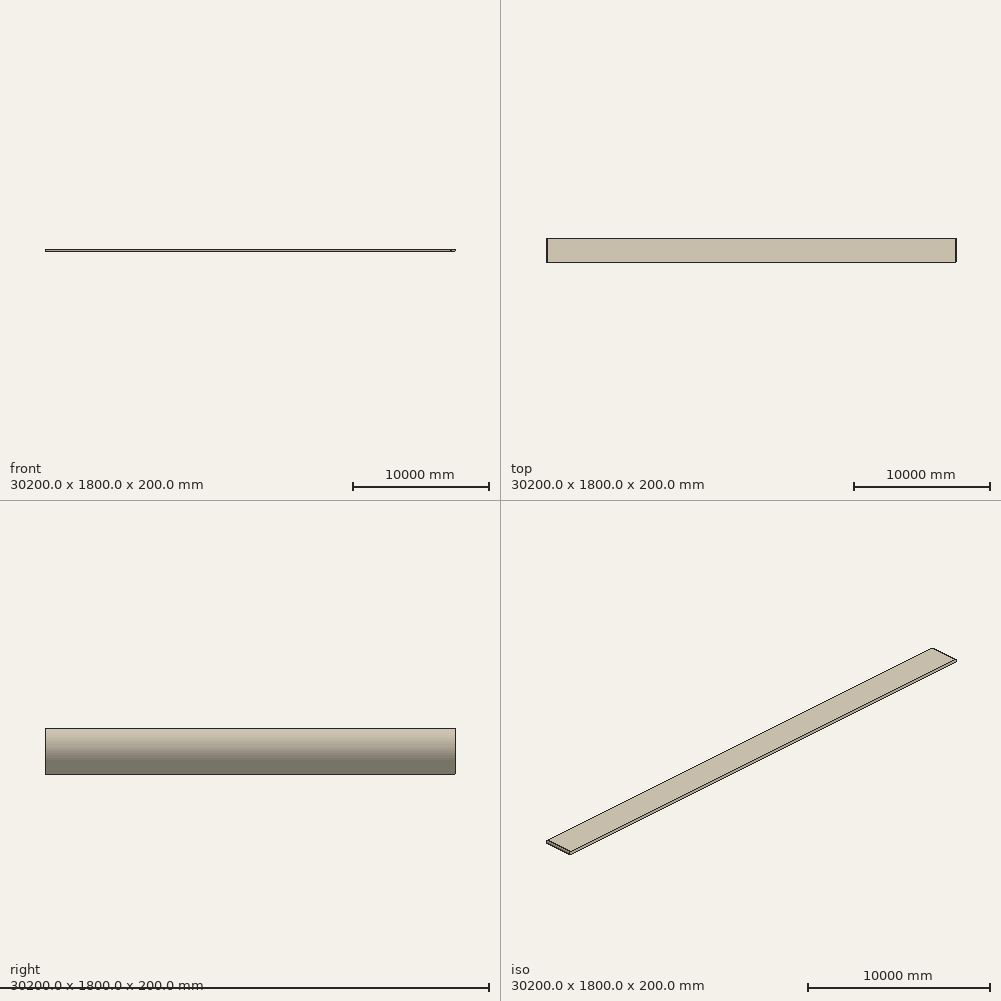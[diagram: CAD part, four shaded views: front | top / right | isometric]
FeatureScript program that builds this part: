
annotation { "Feature Type Name" : "Feature", "Feature Type Description" : "" }
export const myFeature = defineFeature(function(context is Context, id is Id, definition is map)
    precondition{}
    {
        {
            var Q0;
            Q0=qCreatedBy(makeId("Front.planeOp"),FACE);
            var sketch = newSketch(context, id + "F0", { "sketchPlane" : qUnion([Q0])});
            skCircle(sketch, "E0", {"center": v(0, 0) * mm, "radius": 100 * mm});
            skCircle(sketch, "E1", {"center": v(-30000, 0) * mm, "radius": 100 * mm});
            skLineSegment(sketch, "E2", {"start": v(0, 100) * mm, "end": v(-30000, 100) * mm});
            skLineSegment(sketch, "E3", {"start": v(-30000, -100) * mm, "end": v(0, -100) * mm});
            skSolve(sketch);
        }
        {
            var Q0;
            Q0 = qSketchRegion(id + "F0", true);
            extrude(context, id + "F1", {"entities" : qUnion([Q0]), "depth" : 1800 * mm, "offsetDistance" : 25 * mm});
        }
        {
            var Q0;
            Q0=makeQuery(id+"F1.opExtrude","CAP_FACE",FACE,{"disambiguationData":[OSD([sQuery(id+"F0.wireOp",EDGE,"E0")])],"isStart":true});
            var sketch = newSketch(context, id + "F2", { "sketchPlane" : qUnion([Q0])});
            skLineSegment(sketch, "E4", {"start": v(0, 100) * mm, "end": v(262.3, 100) * mm});
            skLineSegment(sketch, "E5", {"start": v(0, -100) * mm, "end": v(262.3, -100) * mm});
            skCircle(sketch, "E6", {"center": v(262.3, 0) * mm, "radius": 100 * mm});
            skSolve(sketch);
        }
        {
            var Q0;
            {var subQ0=sQuery(id+"F2.wireOp",EDGE,"E6");var subQ1=makeQuery(id+"F2.imprint","INTERSECT",VERTEX,{"derivedFrom":[sQuery(id+"F2.wireOp",EDGE,"E4"),subQ0]});Q0=makeQuery(id+"F2.imprint","IMPRINT",FACE,{"disambiguationData":[TD([[makeQuery(id+"F2.imprint","IMPRINT",EDGE,{"disambiguationData":[TD([[subQ1,-1.0]])],"derivedFrom":subQ0}),1.0]])]});}
            extrude(context, id + "F3", {"entities" : qUnion([Q0]), "oppositeDirection" : true, "depth" : 1800 * mm, "offsetDistance" : 25 * mm});
        }
        {
            var Q0;
            Q0=makeQuery(id+"F1.opExtrude","CAP_FACE",FACE,{"disambiguationData":[OSD([sQuery(id+"F0.wireOp",EDGE,"E0")])],"isStart":true});
            var sketch = newSketch(context, id + "F4", { "sketchPlane" : qUnion([Q0])});
            skLineSegment(sketch, "E7", {"start": v(0, 100) * mm, "end": v(266.34, 100) * mm});
            skLineSegment(sketch, "E8", {"start": v(0, -100) * mm, "end": v(266.34, -100) * mm});
            skSolve(sketch);
        }
        {
            var Q0;
            Q0 = qSketchRegion(id + "F0", true);
            var Q1;
            {var subQ2=sQuery(id+"F4.wireOp",EDGE,"E7");Q1=makeQuery(id+"F4.imprint","IMPRINT",FACE,{"disambiguationData":[TD([[makeQuery(id+"F4.imprint","IMPRINT",EDGE,{"derivedFrom":subQ2}),-1.0]])]});}
            extrude(context, id + "F5", {"entities" : qUnion([Q0, Q1]), "operationType" : NewBodyOperationType.REMOVE, "oppositeDirection" : true, "depth" : 1800 * mm, "offsetDistance" : 25 * mm});
        }
    });
